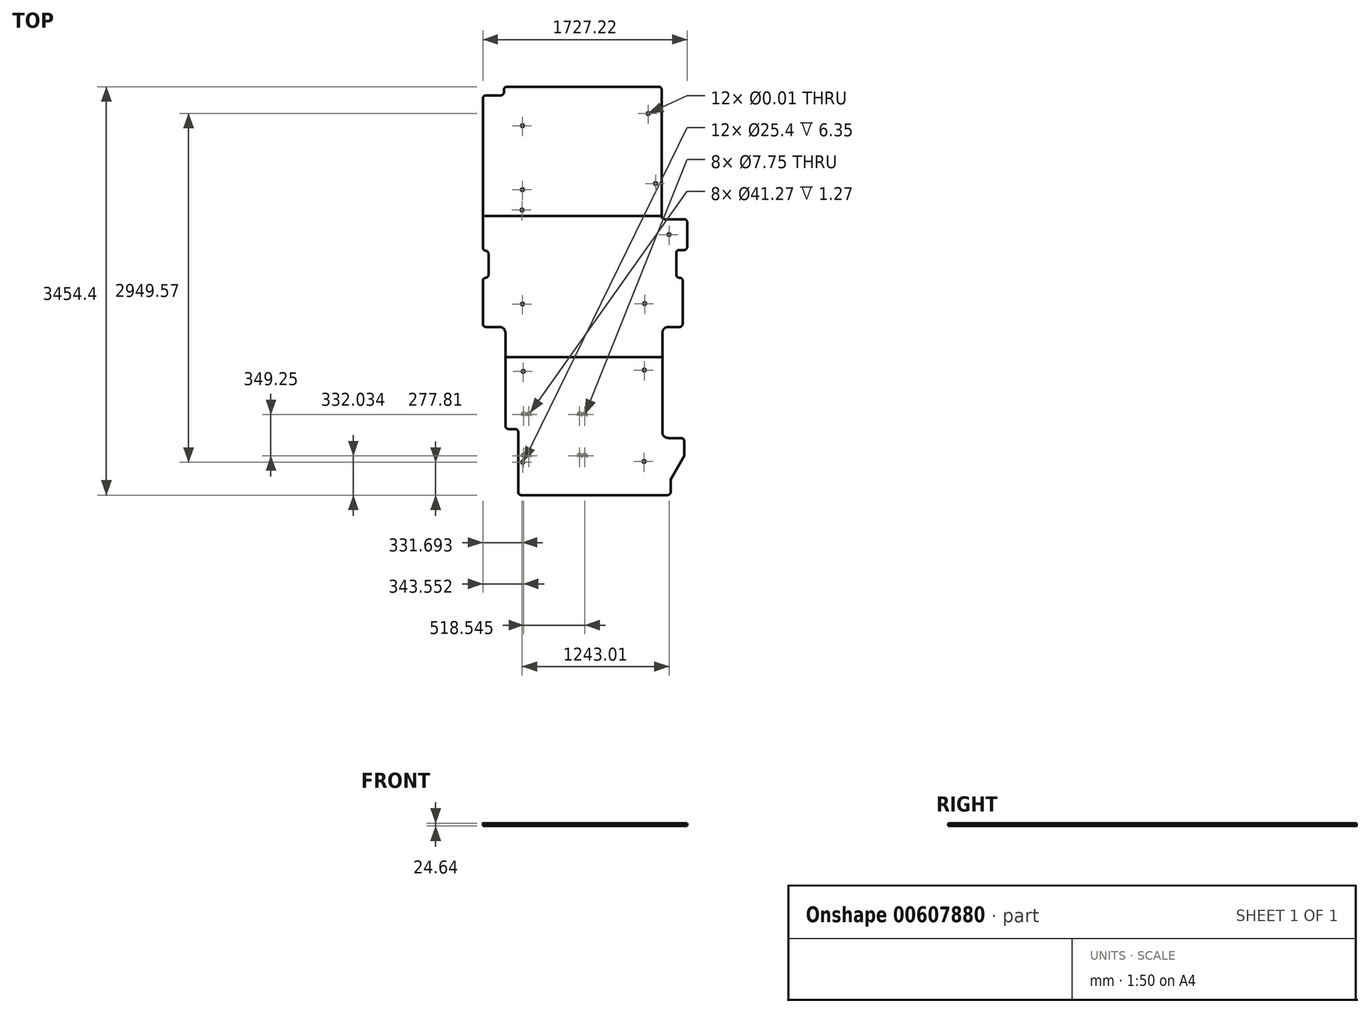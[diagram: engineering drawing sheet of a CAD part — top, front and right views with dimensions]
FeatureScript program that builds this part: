
annotation { "Feature Type Name" : "Feature", "Feature Type Description" : "" }
export const myFeature = defineFeature(function(context is Context, id is Id, definition is map)
    precondition{}
    {
        {
            var Q0;
            Q0=qCreatedBy(makeId("Top.planeOp"),FACE);
            var sketch = newSketch(context, id + "F0", { "sketchPlane" : qUnion([Q0])});
            skLineSegment(sketch, "E0", {"start": v(622, 1725.42) * mm, "end": v(-660.8, 1725.42) * mm});
            skLineSegment(sketch, "E1", {"start": v(-686.2, 1700.02) * mm, "end": v(-686.2, 1677.8) * mm});
            skLineSegment(sketch, "E2", {"start": v(-711.6, 1652.4) * mm, "end": v(-838.6, 1652.4) * mm});
            skLineSegment(sketch, "E3", {"start": v(-863.96, 1627) * mm, "end": v(-863.96, 361.03) * mm});
            skLineSegment(sketch, "E4", {"start": v(-816.67, 312.77) * mm, "end": v(-816.67, 131.63) * mm});
            skLineSegment(sketch, "E5", {"start": v(-863.97, 83.94) * mm, "end": v(-863.97, -281.16) * mm});
            skLineSegment(sketch, "E6", {"start": v(-838.58, -306.84) * mm, "end": v(-724.28, -306.84) * mm});
            skLineSegment(sketch, "E7", {"start": v(-673.57, -357.64) * mm, "end": v(-673.57, -1145) * mm});
            skLineSegment(sketch, "E8", {"start": v(-648.18, -1170.18) * mm, "end": v(-591.03, -1170.18) * mm});
            skLineSegment(sketch, "E9", {"start": v(-565.62, -1195.58) * mm, "end": v(-565.62, -1703.56) * mm});
            skLineSegment(sketch, "E10", {"start": v(-540.23, -1728.98) * mm, "end": v(697.96, -1728.98) * mm});
            skLineSegment(sketch, "E11", {"start": v(723.43, -1703.58) * mm, "end": v(723.43, -1595.63) * mm});
            skLineSegment(sketch, "E12", {"start": v(812.33, -1246.38) * mm, "end": v(704.37, -1246.38) * mm});
            skLineSegment(sketch, "E13", {"start": v(653.58, -1195.58) * mm, "end": v(653.58, -357.64) * mm});
            skLineSegment(sketch, "E14", {"start": v(704.37, -306.58) * mm, "end": v(799.73, -306.58) * mm});
            skLineSegment(sketch, "E15", {"start": v(825.13, -281.18) * mm, "end": v(825.13, 83.94) * mm});
            skLineSegment(sketch, "E16", {"start": v(799.73, 109.34) * mm, "end": v(799.73, 109.34) * mm});
            skLineSegment(sketch, "E17", {"start": v(770.83, 134.74) * mm, "end": v(770.83, 318.9) * mm});
            skLineSegment(sketch, "E18", {"start": v(796.23, 344.3) * mm, "end": v(838, 344.3) * mm});
            skLineSegment(sketch, "E19", {"start": v(863.24, 369.7) * mm, "end": v(863.24, 581.9) * mm});
            skLineSegment(sketch, "E20", {"start": v(837.98, 604.64) * mm, "end": v(672.37, 604.64) * mm});
            skLineSegment(sketch, "E21", {"start": v(647.34, 630.04) * mm, "end": v(647.34, 1700.02) * mm});
            skLineSegment(sketch, "E22", {"start": v(761.68, 101.86) * mm, "end": v(761.68, 126.73) * mm});
            skLineSegment(sketch, "E23", {"start": v(774.95, 114.3) * mm, "end": v(749.02, 114.3) * mm});
            skLineSegment(sketch, "E24", {"start": v(553.55, 101.86) * mm, "end": v(553.55, 126.73) * mm});
            skLineSegment(sketch, "E25", {"start": v(566.82, 114.3) * mm, "end": v(540.9, 114.3) * mm});
            skLineSegment(sketch, "E26", {"start": v(-25.83, -228.32) * mm, "end": v(-25.83, -203.45) * mm});
            skLineSegment(sketch, "E27", {"start": v(-12.56, -215.89) * mm, "end": v(-38.49, -215.89) * mm});
            skLineSegment(sketch, "E28", {"start": v(-233.72, -228.32) * mm, "end": v(-233.72, -203.45) * mm});
            skLineSegment(sketch, "E29", {"start": v(-220.46, -215.89) * mm, "end": v(-246.38, -215.89) * mm});
            skLineSegment(sketch, "E30", {"start": v(-489, -228.32) * mm, "end": v(-489, -203.45) * mm});
            skLineSegment(sketch, "E31", {"start": v(-475.74, -215.89) * mm, "end": v(-501.66, -215.89) * mm});
            skLineSegment(sketch, "E32", {"start": v(-151.41, -1066.48) * mm, "end": v(-151.41, -1041.61) * mm});
            skLineSegment(sketch, "E33", {"start": v(-138.14, -1054.05) * mm, "end": v(-164.07, -1054.05) * mm});
            skLineSegment(sketch, "E34", {"start": v(57.2, -1066.54) * mm, "end": v(57.2, -1041.67) * mm});
            skLineSegment(sketch, "E35", {"start": v(70.47, -1054.1) * mm, "end": v(44.54, -1054.1) * mm});
            skLineSegment(sketch, "E36", {"start": v(-406.13, -1066.48) * mm, "end": v(-406.13, -1041.61) * mm});
            skLineSegment(sketch, "E37", {"start": v(-392.86, -1054.05) * mm, "end": v(-418.79, -1054.05) * mm});
            skLineSegment(sketch, "E38", {"start": v(554, -698.2) * mm, "end": v(554, -673.32) * mm});
            skLineSegment(sketch, "E39", {"start": v(567.26, -685.76) * mm, "end": v(541.33, -685.76) * mm});
            skLineSegment(sketch, "E40", {"start": v(-95.2, 571.74) * mm, "end": v(-95.2, 596.6) * mm});
            skLineSegment(sketch, "E41", {"start": v(-81.93, 584.17) * mm, "end": v(-107.86, 584.17) * mm});
            skLineSegment(sketch, "E42", {"start": v(-523.82, 571.74) * mm, "end": v(-523.82, 596.6) * mm});
            skLineSegment(sketch, "E43", {"start": v(-510.55, 584.17) * mm, "end": v(-536.48, 584.17) * mm});
            skLineSegment(sketch, "E44", {"start": v(-542.82, 1403.54) * mm, "end": v(-542.82, 1428.41) * mm});
            skLineSegment(sketch, "E45", {"start": v(-529.56, 1415.98) * mm, "end": v(-555.48, 1415.98) * mm});
            skLineSegment(sketch, "E46", {"start": v(-114.22, 1402.96) * mm, "end": v(-114.22, 1428.41) * mm});
            skLineSegment(sketch, "E47", {"start": v(-100.95, 1415.98) * mm, "end": v(-126.88, 1415.98) * mm});
            skArc(sketch, "E48", {"start": v(-838.82, 109.34) * mm, "mid": v(-856.62, 101.82) * mm, "end": v(-863.97, 83.94) * mm});
            skArc(sketch, "E49", {"start": v(-838.82, 109.34) * mm, "mid": v(-823.88, 116.65) * mm, "end": v(-816.67, 131.63) * mm});
            skArc(sketch, "E50", {"start": v(-863.96, 361.03) * mm, "mid": v(-855.79, 344.58) * mm, "end": v(-838.67, 337.94) * mm});
            skArc(sketch, "E51", {"start": v(-816.67, 312.77) * mm, "mid": v(-822.94, 329.49) * mm, "end": v(-838.67, 337.94) * mm});
            skArc(sketch, "E52", {"start": v(-838.6, 1652.4) * mm, "mid": v(-856.53, 1644.94) * mm, "end": v(-863.96, 1627) * mm});
            skArc(sketch, "E53", {"start": v(-711.6, 1652.4) * mm, "mid": v(-693.65, 1659.83) * mm, "end": v(-686.2, 1677.8) * mm});
            skArc(sketch, "E54", {"start": v(647.34, 1700.02) * mm, "mid": v(639.92, 1717.96) * mm, "end": v(622, 1725.42) * mm});
            skArc(sketch, "E55", {"start": v(647.34, 630.04) * mm, "mid": v(654.65, 612.2) * mm, "end": v(672.37, 604.64) * mm});
            skArc(sketch, "E56", {"start": v(863.24, 581.9) * mm, "mid": v(854.98, 598.12) * mm, "end": v(837.98, 604.64) * mm});
            skArc(sketch, "E57", {"start": v(838, 344.3) * mm, "mid": v(855.85, 351.78) * mm, "end": v(863.24, 369.7) * mm});
            skArc(sketch, "E58", {"start": v(796.23, 344.3) * mm, "mid": v(778.27, 336.85) * mm, "end": v(770.83, 318.9) * mm});
            skArc(sketch, "E59", {"start": v(825.13, 83.94) * mm, "mid": v(817.69, 101.9) * mm, "end": v(799.73, 109.34) * mm});
            skArc(sketch, "E60", {"start": v(837.73, -1271.79) * mm, "mid": v(830.29, -1253.82) * mm, "end": v(812.33, -1246.38) * mm});
            skArc(sketch, "E61", {"start": v(697.96, -1728.98) * mm, "mid": v(715.96, -1721.57) * mm, "end": v(723.43, -1703.58) * mm});
            skArc(sketch, "E62", {"start": v(-565.62, -1703.56) * mm, "mid": v(-558.2, -1721.53) * mm, "end": v(-540.22, -1728.98) * mm});
            skArc(sketch, "E63", {"start": v(-673.57, -357.64) * mm, "mid": v(-688.42, -321.75) * mm, "end": v(-724.28, -306.84) * mm});
            skLineSegment(sketch, "E64", {"start": v(723.43, -1595.63) * mm, "end": v(837.73, -1395.6) * mm});
            skLineSegment(sketch, "E65", {"start": v(837.73, -1271.79) * mm, "end": v(837.73, -1395.6) * mm});
            skArc(sketch, "E66", {"start": v(-863.97, -281.16) * mm, "mid": v(-856.63, -299.3) * mm, "end": v(-838.58, -306.84) * mm});
            skArc(sketch, "E67", {"start": v(770.83, 134.74) * mm, "mid": v(778.27, 116.78) * mm, "end": v(796.23, 109.34) * mm});
            skLineSegment(sketch, "E68", {"start": v(796.23, 109.34) * mm, "end": v(799.73, 109.34) * mm});
            skArc(sketch, "E69", {"start": v(653.58, -1195.58) * mm, "mid": v(668.45, -1231.5) * mm, "end": v(704.37, -1246.38) * mm});
            skArc(sketch, "E70", {"start": v(799.73, -306.58) * mm, "mid": v(817.69, -299.14) * mm, "end": v(825.13, -281.18) * mm});
            skArc(sketch, "E71", {"start": v(704.37, -306.58) * mm, "mid": v(668.36, -321.55) * mm, "end": v(653.58, -357.64) * mm});
            skArc(sketch, "E72", {"start": v(-565.62, -1195.58) * mm, "mid": v(-573.07, -1177.62) * mm, "end": v(-591.03, -1170.18) * mm});
            skArc(sketch, "E73", {"start": v(-673.57, -1145) * mm, "mid": v(-666.06, -1162.82) * mm, "end": v(-648.18, -1170.18) * mm});
            skArc(sketch, "E74", {"start": v(-660.8, 1725.42) * mm, "mid": v(-678.77, 1717.98) * mm, "end": v(-686.2, 1700.02) * mm});
            skSolve(sketch);
        }
        {
            var Q0;
            Q0=makeQuery(id+"F0.imprint","IMPRINT",FACE,{"disambiguationData":[TD([[makeQuery(id+"F0.imprint","IMPRINT",EDGE,{"derivedFrom":sQuery(id+"F0.wireOp",EDGE,"E0")}),1.0]])]});
            extrude(context, id + "F1", {"entities" : qUnion([Q0]), "depth" : 24.64 * mm, "offsetDistance" : 25.4 * mm});
        }
        {
            var Q0;
            Q0=makeQuery(id+"F1.opExtrude","CAP_FACE",FACE,{"disambiguationData":[OSD([sQuery(id+"F0.wireOp",EDGE,"E0"),sQuery(id+"F0.wireOp",EDGE,"E1"),sQuery(id+"F0.wireOp",EDGE,"E2"),sQuery(id+"F0.wireOp",EDGE,"E3"),sQuery(id+"F0.wireOp",EDGE,"E4"),sQuery(id+"F0.wireOp",EDGE,"E5"),sQuery(id+"F0.wireOp",EDGE,"E6"),sQuery(id+"F0.wireOp",EDGE,"E7"),sQuery(id+"F0.wireOp",EDGE,"E8"),sQuery(id+"F0.wireOp",EDGE,"E9"),sQuery(id+"F0.wireOp",EDGE,"E10"),sQuery(id+"F0.wireOp",EDGE,"E11"),sQuery(id+"F0.wireOp",EDGE,"E12"),sQuery(id+"F0.wireOp",EDGE,"E13"),sQuery(id+"F0.wireOp",EDGE,"E14"),sQuery(id+"F0.wireOp",EDGE,"E15"),sQuery(id+"F0.wireOp",EDGE,"E17"),sQuery(id+"F0.wireOp",EDGE,"E18"),sQuery(id+"F0.wireOp",EDGE,"E19"),sQuery(id+"F0.wireOp",EDGE,"E20"),sQuery(id+"F0.wireOp",EDGE,"E21"),sQuery(id+"F0.wireOp",EDGE,"E48"),sQuery(id+"F0.wireOp",EDGE,"E49"),sQuery(id+"F0.wireOp",EDGE,"E50"),sQuery(id+"F0.wireOp",EDGE,"E51"),sQuery(id+"F0.wireOp",EDGE,"E52"),sQuery(id+"F0.wireOp",EDGE,"E53"),sQuery(id+"F0.wireOp",EDGE,"E54"),sQuery(id+"F0.wireOp",EDGE,"E55"),sQuery(id+"F0.wireOp",EDGE,"E56"),sQuery(id+"F0.wireOp",EDGE,"E57"),sQuery(id+"F0.wireOp",EDGE,"E58"),sQuery(id+"F0.wireOp",EDGE,"E59"),sQuery(id+"F0.wireOp",EDGE,"E60"),sQuery(id+"F0.wireOp",EDGE,"E61"),sQuery(id+"F0.wireOp",EDGE,"E62"),sQuery(id+"F0.wireOp",EDGE,"E63"),sQuery(id+"F0.wireOp",EDGE,"E64"),sQuery(id+"F0.wireOp",EDGE,"E65"),sQuery(id+"F0.wireOp",EDGE,"E66"),sQuery(id+"F0.wireOp",EDGE,"E67"),sQuery(id+"F0.wireOp",EDGE,"E68"),sQuery(id+"F0.wireOp",EDGE,"E69"),sQuery(id+"F0.wireOp",EDGE,"E70"),sQuery(id+"F0.wireOp",EDGE,"E71"),sQuery(id+"F0.wireOp",EDGE,"E72"),sQuery(id+"F0.wireOp",EDGE,"E73"),sQuery(id+"F0.wireOp",EDGE,"E74")])],"isStart":false});
            var sketch = newSketch(context, id + "F2", { "sketchPlane" : qUnion([Q0])});
            skPoint(sketch, "E75", {"position": v(-542.52, 1415.98) * mm});
            skPoint(sketch, "E76", {"position": v(-113.92, 1415.98) * mm});
            skPoint(sketch, "E77", {"position": v(-94.9, 584.17) * mm});
            skPoint(sketch, "E78", {"position": v(-523.51, 584.17) * mm});
            skPoint(sketch, "E79", {"position": v(-488.7, -215.89) * mm});
            skPoint(sketch, "E80", {"position": v(-233.72, -215.89) * mm});
            skPoint(sketch, "E81", {"position": v(-25.83, -215.89) * mm});
            skPoint(sketch, "E82", {"position": v(553.86, 114.3) * mm});
            skPoint(sketch, "E83", {"position": v(761.99, 114.3) * mm});
            skPoint(sketch, "E84", {"position": v(554.3, -685.76) * mm});
            skPoint(sketch, "E85", {"position": v(57.5, -1054.1) * mm});
            skPoint(sketch, "E86", {"position": v(-151.1, -1054.05) * mm});
            skPoint(sketch, "E87", {"position": v(-406.13, -1054.05) * mm});
            skPoint(sketch, "E88", {"position": v(-542.52, 1284.21) * mm});
            skPoint(sketch, "E89", {"position": v(-542.52, 958.78) * mm});
            skPoint(sketch, "E90", {"position": v(-113.92, 1284.2) * mm});
            skPoint(sketch, "E91", {"position": v(-113.92, 958.78) * mm});
            skPoint(sketch, "E92", {"position": v(-523.51, 452.4) * mm});
            skPoint(sketch, "E93", {"position": v(-523.51, 126.97) * mm});
            skPoint(sketch, "E94", {"position": v(-94.9, 452.4) * mm});
            skPoint(sketch, "E95", {"position": v(-94.9, 126.97) * mm});
            skPoint(sketch, "E96", {"position": v(553.86, -17.48) * mm});
            skPoint(sketch, "E97", {"position": v(553.86, -342.9) * mm});
            skPoint(sketch, "E98", {"position": v(761.99, -17.48) * mm});
            skPoint(sketch, "E99", {"position": v(-488.7, -347.66) * mm});
            skPoint(sketch, "E100", {"position": v(-488.7, -673.09) * mm});
            skPoint(sketch, "E101", {"position": v(-233.72, -347.66) * mm});
            skPoint(sketch, "E102", {"position": v(-233.72, -673.09) * mm});
            skPoint(sketch, "E103", {"position": v(-25.83, -347.66) * mm});
            skPoint(sketch, "E104", {"position": v(-25.83, -673.09) * mm});
            skPoint(sketch, "E105", {"position": v(553.86, -817.53) * mm});
            skPoint(sketch, "E106", {"position": v(554.3, -1142.96) * mm});
            skSolve(sketch);
        }
        {
            var Q0;
            Q0=makeQuery(id+"F1.opExtrude","CAP_FACE",FACE,{"disambiguationData":[OSD([sQuery(id+"F0.wireOp",EDGE,"E0"),sQuery(id+"F0.wireOp",EDGE,"E1"),sQuery(id+"F0.wireOp",EDGE,"E2"),sQuery(id+"F0.wireOp",EDGE,"E3"),sQuery(id+"F0.wireOp",EDGE,"E4"),sQuery(id+"F0.wireOp",EDGE,"E5"),sQuery(id+"F0.wireOp",EDGE,"E6"),sQuery(id+"F0.wireOp",EDGE,"E7"),sQuery(id+"F0.wireOp",EDGE,"E8"),sQuery(id+"F0.wireOp",EDGE,"E9"),sQuery(id+"F0.wireOp",EDGE,"E10"),sQuery(id+"F0.wireOp",EDGE,"E11"),sQuery(id+"F0.wireOp",EDGE,"E12"),sQuery(id+"F0.wireOp",EDGE,"E13"),sQuery(id+"F0.wireOp",EDGE,"E14"),sQuery(id+"F0.wireOp",EDGE,"E15"),sQuery(id+"F0.wireOp",EDGE,"E17"),sQuery(id+"F0.wireOp",EDGE,"E18"),sQuery(id+"F0.wireOp",EDGE,"E19"),sQuery(id+"F0.wireOp",EDGE,"E20"),sQuery(id+"F0.wireOp",EDGE,"E21"),sQuery(id+"F0.wireOp",EDGE,"E48"),sQuery(id+"F0.wireOp",EDGE,"E49"),sQuery(id+"F0.wireOp",EDGE,"E50"),sQuery(id+"F0.wireOp",EDGE,"E51"),sQuery(id+"F0.wireOp",EDGE,"E52"),sQuery(id+"F0.wireOp",EDGE,"E53"),sQuery(id+"F0.wireOp",EDGE,"E54"),sQuery(id+"F0.wireOp",EDGE,"E55"),sQuery(id+"F0.wireOp",EDGE,"E56"),sQuery(id+"F0.wireOp",EDGE,"E57"),sQuery(id+"F0.wireOp",EDGE,"E58"),sQuery(id+"F0.wireOp",EDGE,"E59"),sQuery(id+"F0.wireOp",EDGE,"E60"),sQuery(id+"F0.wireOp",EDGE,"E61"),sQuery(id+"F0.wireOp",EDGE,"E62"),sQuery(id+"F0.wireOp",EDGE,"E63"),sQuery(id+"F0.wireOp",EDGE,"E64"),sQuery(id+"F0.wireOp",EDGE,"E65"),sQuery(id+"F0.wireOp",EDGE,"E66"),sQuery(id+"F0.wireOp",EDGE,"E67"),sQuery(id+"F0.wireOp",EDGE,"E68"),sQuery(id+"F0.wireOp",EDGE,"E69"),sQuery(id+"F0.wireOp",EDGE,"E70"),sQuery(id+"F0.wireOp",EDGE,"E71"),sQuery(id+"F0.wireOp",EDGE,"E72"),sQuery(id+"F0.wireOp",EDGE,"E73"),sQuery(id+"F0.wireOp",EDGE,"E74")])],"isStart":false});
            var sketch = newSketch(context, id + "F3", { "sketchPlane" : qUnion([Q0])});
            skLineSegment(sketch, "E107", {"start": v(-121.12, -1728.98) * mm, "end": v(-121.12, 1725.42) * mm, "construction": true});
            skPoint(sketch, "E108", {"position": v(-527.52, -1451.17) * mm});
            skPoint(sketch, "E109", {"position": v(-522.76, -682.82) * mm});
            skPoint(sketch, "E110", {"position": v(-529.11, -112.9) * mm});
            skPoint(sketch, "E111", {"position": v(-532.29, 682.43) * mm});
            skPoint(sketch, "E112", {"position": v(-529.11, 853.88) * mm});
            skPoint(sketch, "E113", {"position": v(-529.11, 1395.22) * mm});
            skPoint(sketch, "E114", {"position": v(534.51, 1498.4) * mm});
            skPoint(sketch, "E115", {"position": v(596.43, 906.27) * mm});
            skPoint(sketch, "E116", {"position": v(710.73, 474.47) * mm});
            skPoint(sketch, "E117", {"position": v(504.35, -109.73) * mm});
            skPoint(sketch, "E118", {"position": v(501.18, -671.7) * mm});
            skPoint(sketch, "E119", {"position": v(499.59, -1444.82) * mm});
            skLineSegment(sketch, "E120", {"start": v(-802.03, -1728.98) * mm, "end": v(848.13, -1728.98) * mm, "construction": true});
            skSolve(sketch);
        }
        {
            var Q0;
            Q0=sQuery(id+"F3.wireOp",VERTEX,"E113");
            var Q1;
            Q1=sQuery(id+"F3.wireOp",VERTEX,"E114");
            var Q2;
            Q2=sQuery(id+"F3.wireOp",VERTEX,"E115");
            var Q3;
            Q3=sQuery(id+"F3.wireOp",VERTEX,"E112");
            var Q4;
            Q4=sQuery(id+"F3.wireOp",VERTEX,"E111");
            var Q5;
            Q5=sQuery(id+"F3.wireOp",VERTEX,"E116");
            var Q6;
            Q6=sQuery(id+"F3.wireOp",VERTEX,"E117");
            var Q7;
            Q7=sQuery(id+"F3.wireOp",VERTEX,"E110");
            var Q8;
            Q8=sQuery(id+"F3.wireOp",VERTEX,"E109");
            var Q9;
            Q9=sQuery(id+"F3.wireOp",VERTEX,"E118");
            var Q10;
            Q10=sQuery(id+"F3.wireOp",VERTEX,"E119");
            var Q11;
            Q11=sQuery(id+"F3.wireOp",VERTEX,"E108");
            var Q12;
            Q12=makeQuery(id+"F1.opExtrude","SWEPT_BODY",BODY,{"disambiguationData":[OSD([sQuery(id+"F0.wireOp",EDGE,"E0"),sQuery(id+"F0.wireOp",EDGE,"E1"),sQuery(id+"F0.wireOp",EDGE,"E2"),sQuery(id+"F0.wireOp",EDGE,"E3"),sQuery(id+"F0.wireOp",EDGE,"E4"),sQuery(id+"F0.wireOp",EDGE,"E5"),sQuery(id+"F0.wireOp",EDGE,"E6"),sQuery(id+"F0.wireOp",EDGE,"E7"),sQuery(id+"F0.wireOp",EDGE,"E8"),sQuery(id+"F0.wireOp",EDGE,"E9"),sQuery(id+"F0.wireOp",EDGE,"E10"),sQuery(id+"F0.wireOp",EDGE,"E11"),sQuery(id+"F0.wireOp",EDGE,"E12"),sQuery(id+"F0.wireOp",EDGE,"E13"),sQuery(id+"F0.wireOp",EDGE,"E14"),sQuery(id+"F0.wireOp",EDGE,"E15"),sQuery(id+"F0.wireOp",EDGE,"E17"),sQuery(id+"F0.wireOp",EDGE,"E18"),sQuery(id+"F0.wireOp",EDGE,"E19"),sQuery(id+"F0.wireOp",EDGE,"E20"),sQuery(id+"F0.wireOp",EDGE,"E21"),sQuery(id+"F0.wireOp",EDGE,"E48"),sQuery(id+"F0.wireOp",EDGE,"E49"),sQuery(id+"F0.wireOp",EDGE,"E50"),sQuery(id+"F0.wireOp",EDGE,"E51"),sQuery(id+"F0.wireOp",EDGE,"E52"),sQuery(id+"F0.wireOp",EDGE,"E53"),sQuery(id+"F0.wireOp",EDGE,"E54"),sQuery(id+"F0.wireOp",EDGE,"E55"),sQuery(id+"F0.wireOp",EDGE,"E56"),sQuery(id+"F0.wireOp",EDGE,"E57"),sQuery(id+"F0.wireOp",EDGE,"E58"),sQuery(id+"F0.wireOp",EDGE,"E59"),sQuery(id+"F0.wireOp",EDGE,"E60"),sQuery(id+"F0.wireOp",EDGE,"E61"),sQuery(id+"F0.wireOp",EDGE,"E62"),sQuery(id+"F0.wireOp",EDGE,"E63"),sQuery(id+"F0.wireOp",EDGE,"E64"),sQuery(id+"F0.wireOp",EDGE,"E65"),sQuery(id+"F0.wireOp",EDGE,"E66"),sQuery(id+"F0.wireOp",EDGE,"E67"),sQuery(id+"F0.wireOp",EDGE,"E68"),sQuery(id+"F0.wireOp",EDGE,"E69"),sQuery(id+"F0.wireOp",EDGE,"E70"),sQuery(id+"F0.wireOp",EDGE,"E71"),sQuery(id+"F0.wireOp",EDGE,"E72"),sQuery(id+"F0.wireOp",EDGE,"E73"),sQuery(id+"F0.wireOp",EDGE,"E74")])]});
            hole(context, id + "F4", {"style" : HoleStyle.C_BORE, "endStyle" : HoleEndStyle.THROUGH, "holeDiameter" : 3 / 203.2 * mm, "cBoreDiameter" : 25.4 * mm, "cBoreDepth" : 6.35 * mm, "majorDiameter" : 6.35 * mm, "isTappedThrough" : true, "tappedDepth" : 12.7 * mm, "tapClearance" : 3, "locations" : qUnion([Q0, Q1, Q2, Q3, Q4, Q5, Q6, Q7, Q8, Q9, Q10, Q11]), "scope" : qUnion([Q12])});
        }
        {
            var Q0;
            Q0=makeQuery(id+"F2.imprint","IMPRINT",FACE,{"disambiguationData":[TD([[makeQuery(id+"F2.imprint","IMPRINT",EDGE,{"derivedFrom":makeQuery(id+"F1.opExtrude","CAP_EDGE",EDGE,{"disambiguationData":[OSD([sQuery(id+"F0.wireOp",EDGE,"E0")])],"isStart":false})}),1.0]])]});
            var sketch = newSketch(context, id + "F5", { "sketchPlane" : qUnion([Q0])});
            skLineSegment(sketch, "E121.bottom", {"start": v(-912.85, -560.56) * mm, "end": v(1341.93, -560.56) * mm});
            skLineSegment(sketch, "E121.top", {"start": v(-912.85, -560.58) * mm, "end": v(1341.93, -560.58) * mm});
            skLineSegment(sketch, "E121.left", {"start": v(-912.85, -560.56) * mm, "end": v(-912.85, -560.58) * mm});
            skLineSegment(sketch, "E121.right", {"start": v(1341.93, -560.56) * mm, "end": v(1341.93, -560.58) * mm});
            skLineSegment(sketch, "E122.bottom", {"start": v(-1134.08, 633.24) * mm, "end": v(1278.6, 633.24) * mm});
            skLineSegment(sketch, "E122.top", {"start": v(-1134.08, 633.22) * mm, "end": v(1278.6, 633.22) * mm});
            skLineSegment(sketch, "E122.left", {"start": v(-1134.08, 633.24) * mm, "end": v(-1134.08, 633.22) * mm});
            skLineSegment(sketch, "E122.right", {"start": v(1278.6, 633.24) * mm, "end": v(1278.6, 633.22) * mm});
            skSolve(sketch);
        }
        {
            var Q0;
            Q0 = qSketchRegion(id + "F5", true);
            extrude(context, id + "F6", {"entities" : qUnion([Q0]), "operationType" : NewBodyOperationType.REMOVE, "endBound" : BoundingType.THROUGH_ALL, "oppositeDirection" : true, "depth" : 25.4 * mm, "offsetDistance" : 25.4 * mm});
        }
        {
            var Q0;
            Q0=makeQuery(id+"F2.imprint","IMPRINT",FACE,{"disambiguationData":[TD([[makeQuery(id+"F2.imprint","IMPRINT",EDGE,{"derivedFrom":makeQuery(id+"F1.opExtrude","CAP_EDGE",EDGE,{"disambiguationData":[OSD([sQuery(id+"F0.wireOp",EDGE,"E0")])],"isStart":false})}),1.0]])]});
            var sketch = newSketch(context, id + "F7", { "sketchPlane" : qUnion([Q0])});
            skLineSegment(sketch, "E123", {"start": v(-771.4, -1047.7) * mm, "end": v(120.5, -1047.7) * mm, "construction": true});
            skPoint(sketch, "E124", {"position": v(-520.43, -1047.7) * mm});
            skPoint(sketch, "E125", {"position": v(-475.98, -1047.7) * mm});
            skPoint(sketch, "E126", {"position": v(-46.33, -1047.7) * mm});
            skPoint(sketch, "E127", {"position": v(-1.88, -1047.7) * mm});
            skPoint(sketch, "E128", {"position": v(-520.43, -1396.95) * mm});
            skPoint(sketch, "E129", {"position": v(-475.98, -1396.95) * mm});
            skPoint(sketch, "E130", {"position": v(-46.33, -1396.95) * mm});
            skPoint(sketch, "E131", {"position": v(-1.88, -1396.95) * mm});
            skSolve(sketch);
        }
        {
            var Q0;
            {var subQ0=sQuery(id+"F0.wireOp",EDGE,"E73");var subQ1=sQuery(id+"F0.wireOp",EDGE,"E72");var subQ2=sQuery(id+"F0.wireOp",EDGE,"E69");var subQ3=sQuery(id+"F0.wireOp",EDGE,"E65");var subQ4=sQuery(id+"F0.wireOp",EDGE,"E13");var subQ5=sQuery(id+"F0.wireOp",EDGE,"E64");var subQ6=sQuery(id+"F0.wireOp",EDGE,"E9");var subQ7=sQuery(id+"F0.wireOp",EDGE,"E8");var subQ8=sQuery(id+"F0.wireOp",EDGE,"E7");var subQ9=sQuery(id+"F0.wireOp",EDGE,"E10");var subQ10=sQuery(id+"F0.wireOp",EDGE,"E60");var subQ11=sQuery(id+"F0.wireOp",EDGE,"E11");var subQ12=sQuery(id+"F0.wireOp",EDGE,"E61");var subQ13=sQuery(id+"F0.wireOp",EDGE,"E12");var subQ14=sQuery(id+"F0.wireOp",EDGE,"E62");Q0=makeQuery(id+"F6.boolean.opBoolean","SPLIT",FACE,{"disambiguationData":[TD([makeQuery(id+"F1.opExtrude","SWEPT_FACE",FACE,{"disambiguationData":[OSD([subQ7])]})])],"derivedFrom":makeQuery(id+"F1.opExtrude","CAP_FACE",FACE,{"disambiguationData":[OSD([sQuery(id+"F0.wireOp",EDGE,"E0"),sQuery(id+"F0.wireOp",EDGE,"E1"),sQuery(id+"F0.wireOp",EDGE,"E2"),sQuery(id+"F0.wireOp",EDGE,"E3"),sQuery(id+"F0.wireOp",EDGE,"E4"),sQuery(id+"F0.wireOp",EDGE,"E5"),sQuery(id+"F0.wireOp",EDGE,"E6"),subQ8,subQ7,subQ6,subQ9,subQ11,subQ13,subQ4,sQuery(id+"F0.wireOp",EDGE,"E14"),sQuery(id+"F0.wireOp",EDGE,"E15"),sQuery(id+"F0.wireOp",EDGE,"E17"),sQuery(id+"F0.wireOp",EDGE,"E18"),sQuery(id+"F0.wireOp",EDGE,"E19"),sQuery(id+"F0.wireOp",EDGE,"E20"),sQuery(id+"F0.wireOp",EDGE,"E21"),sQuery(id+"F0.wireOp",EDGE,"E48"),sQuery(id+"F0.wireOp",EDGE,"E49"),sQuery(id+"F0.wireOp",EDGE,"E50"),sQuery(id+"F0.wireOp",EDGE,"E51"),sQuery(id+"F0.wireOp",EDGE,"E52"),sQuery(id+"F0.wireOp",EDGE,"E53"),sQuery(id+"F0.wireOp",EDGE,"E54"),sQuery(id+"F0.wireOp",EDGE,"E55"),sQuery(id+"F0.wireOp",EDGE,"E56"),sQuery(id+"F0.wireOp",EDGE,"E57"),sQuery(id+"F0.wireOp",EDGE,"E58"),sQuery(id+"F0.wireOp",EDGE,"E59"),subQ10,subQ12,subQ14,sQuery(id+"F0.wireOp",EDGE,"E63"),subQ5,subQ3,sQuery(id+"F0.wireOp",EDGE,"E66"),sQuery(id+"F0.wireOp",EDGE,"E67"),sQuery(id+"F0.wireOp",EDGE,"E68"),subQ2,sQuery(id+"F0.wireOp",EDGE,"E70"),sQuery(id+"F0.wireOp",EDGE,"E71"),subQ1,subQ0,sQuery(id+"F0.wireOp",EDGE,"E74")])],"isStart":true})});}
            var sketch = newSketch(context, id + "F8", { "sketchPlane" : qUnion([Q0])});
            skPoint(sketch, "E132.0", {"position": v(-520.43, 1396.95) * mm});
            skPoint(sketch, "E133.0", {"position": v(-475.98, 1396.95) * mm});
            skPoint(sketch, "E134.0", {"position": v(-520.43, 1047.7) * mm});
            skPoint(sketch, "E135.0", {"position": v(-475.98, 1047.7) * mm});
            skPoint(sketch, "E136.0", {"position": v(-46.33, 1047.7) * mm});
            skPoint(sketch, "E137.0", {"position": v(-1.88, 1047.7) * mm});
            skPoint(sketch, "E138.0", {"position": v(-46.33, 1396.95) * mm});
            skPoint(sketch, "E139.0", {"position": v(-1.88, 1396.95) * mm});
            skSolve(sketch);
        }
        {
            var Q0;
            Q0=sQuery(id+"F8.wireOp",VERTEX,"E133.0");
            var Q1;
            Q1=sQuery(id+"F8.wireOp",VERTEX,"E132.0");
            var Q2;
            Q2=sQuery(id+"F8.wireOp",VERTEX,"E138.0");
            var Q3;
            Q3=sQuery(id+"F8.wireOp",VERTEX,"E139.0");
            var Q4;
            Q4=sQuery(id+"F8.wireOp",VERTEX,"E137.0");
            var Q5;
            Q5=sQuery(id+"F8.wireOp",VERTEX,"E136.0");
            var Q6;
            Q6=sQuery(id+"F8.wireOp",VERTEX,"E135.0");
            var Q7;
            Q7=sQuery(id+"F8.wireOp",VERTEX,"E134.0");
            var Q8;
            Q8=makeQuery(id+"F6.boolean.opBoolean","SPLIT",BODY,{"disambiguationData":[OD(1.0)],"derivedFrom":makeQuery(id+"F1.opExtrude","SWEPT_BODY",BODY,{"disambiguationData":[OSD([sQuery(id+"F0.wireOp",EDGE,"E0"),sQuery(id+"F0.wireOp",EDGE,"E1"),sQuery(id+"F0.wireOp",EDGE,"E2"),sQuery(id+"F0.wireOp",EDGE,"E3"),sQuery(id+"F0.wireOp",EDGE,"E4"),sQuery(id+"F0.wireOp",EDGE,"E5"),sQuery(id+"F0.wireOp",EDGE,"E6"),sQuery(id+"F0.wireOp",EDGE,"E7"),sQuery(id+"F0.wireOp",EDGE,"E8"),sQuery(id+"F0.wireOp",EDGE,"E9"),sQuery(id+"F0.wireOp",EDGE,"E10"),sQuery(id+"F0.wireOp",EDGE,"E11"),sQuery(id+"F0.wireOp",EDGE,"E12"),sQuery(id+"F0.wireOp",EDGE,"E13"),sQuery(id+"F0.wireOp",EDGE,"E14"),sQuery(id+"F0.wireOp",EDGE,"E15"),sQuery(id+"F0.wireOp",EDGE,"E17"),sQuery(id+"F0.wireOp",EDGE,"E18"),sQuery(id+"F0.wireOp",EDGE,"E19"),sQuery(id+"F0.wireOp",EDGE,"E20"),sQuery(id+"F0.wireOp",EDGE,"E21"),sQuery(id+"F0.wireOp",EDGE,"E48"),sQuery(id+"F0.wireOp",EDGE,"E49"),sQuery(id+"F0.wireOp",EDGE,"E50"),sQuery(id+"F0.wireOp",EDGE,"E51"),sQuery(id+"F0.wireOp",EDGE,"E52"),sQuery(id+"F0.wireOp",EDGE,"E53"),sQuery(id+"F0.wireOp",EDGE,"E54"),sQuery(id+"F0.wireOp",EDGE,"E55"),sQuery(id+"F0.wireOp",EDGE,"E56"),sQuery(id+"F0.wireOp",EDGE,"E57"),sQuery(id+"F0.wireOp",EDGE,"E58"),sQuery(id+"F0.wireOp",EDGE,"E59"),sQuery(id+"F0.wireOp",EDGE,"E60"),sQuery(id+"F0.wireOp",EDGE,"E61"),sQuery(id+"F0.wireOp",EDGE,"E62"),sQuery(id+"F0.wireOp",EDGE,"E63"),sQuery(id+"F0.wireOp",EDGE,"E64"),sQuery(id+"F0.wireOp",EDGE,"E65"),sQuery(id+"F0.wireOp",EDGE,"E66"),sQuery(id+"F0.wireOp",EDGE,"E67"),sQuery(id+"F0.wireOp",EDGE,"E68"),sQuery(id+"F0.wireOp",EDGE,"E69"),sQuery(id+"F0.wireOp",EDGE,"E70"),sQuery(id+"F0.wireOp",EDGE,"E71"),sQuery(id+"F0.wireOp",EDGE,"E72"),sQuery(id+"F0.wireOp",EDGE,"E73"),sQuery(id+"F0.wireOp",EDGE,"E74")])]})});
            hole(context, id + "F9", {"style" : HoleStyle.C_BORE, "endStyle" : HoleEndStyle.THROUGH, "holeDiameter" : 7.75 * mm, "cBoreDiameter" : 41.27 * mm, "cBoreDepth" : 1.27 * mm, "majorDiameter" : 6.35 * mm, "isTappedThrough" : true, "tappedDepth" : 12.7 * mm, "tapClearance" : 3, "startFromSketch" : true, "locations" : qUnion([Q0, Q1, Q2, Q3, Q4, Q5, Q6, Q7]), "scope" : qUnion([Q8])});
        }
    });
